# Revit family: Gripple UniGrip Kit
name_source: partatom
category: Specialty Equipment
revit_build: Autodesk Revit 2017 (Build: 20160225_1515(x64)
units: mm (PartAtom-declared; Revit-internal decimal feet)

## family parameters
Always vertical = Yes
Cut with Voids When Loaded = No
Part Type = Normal
Room Calculation Point = No
Round Connector Dimension = Use Diameter
Shared = Yes
Work Plane-Based = Yes

## types (3) — shared parameters
D = 4 mm  [stored 0.0131234 ft]
E = 3 mm  [stored 0.00984252 ft]
F = 2 mm  [stored 0.00656168 ft]
Manufacturer = Gripple Ltd
URL = https://www.gripple.com
zero-valued in all types: Default Elevation

## per-type parameters (varying)
| type | A | AF | B | Body Dia | C | G | Hanger SWL (kg) | Model | WD | WD/2 | v | w | y | z |
| UG2 | 10 mm  [stored 0.0328084 ft] | 17 mm  [stored 0.0557743 ft] | 35 mm  [stored 0.114829 ft] | 19 mm  [stored 0.062336 ft] | 2 mm  [stored 0.00656168 ft] | 8 mm  [stored 0.0262467 ft] | 55kg | UniGrip No2 | 2 mm  [stored 0.00656168 ft] | 1 mm  [stored 0.00328084 ft] | 6 mm  [stored 0.019685 ft] | 11 mm | 12 mm  [stored 0.0393701 ft] | 9 mm  [stored 0.0295276 ft] |
| UG3 | 20 mm  [stored 0.0656168 ft] | 17 mm  [stored 0.0557743 ft] | 48 mm | 22 mm | 4 mm  [stored 0.0131234 ft] | 11 mm | 110kg | UniGrip No3 | 3 mm  [stored 0.00984252 ft] | 2 mm  [stored 0.00656168 ft] | 8 mm  [stored 0.0262467 ft] | 11 mm | 14 mm  [stored 0.0459318 ft] | 9 mm  [stored 0.0295276 ft] |
| UG4 | 25 mm  [stored 0.082021 ft] | 22 mm | 57 mm | 30 mm | 4 mm  [stored 0.0131234 ft] | 13 mm | 250kg | UniGrip No4 | 5 mm  [stored 0.0164042 ft] | 2 mm  [stored 0.00656168 ft] | 10 mm  [stored 0.0328084 ft] | 16 mm | 21 mm | 10 mm  [stored 0.0328084 ft] |

note: column(s) folded — value = type name in every type: Assembly Code

note: [stored X ft] marks values corroborated as IEEE doubles in the binary element streams (Revit-internal decimal feet)

## geometry (parser evidence)
native form markers: Blend x2, Sweep x6
no freeform markers — native parametric forms only
